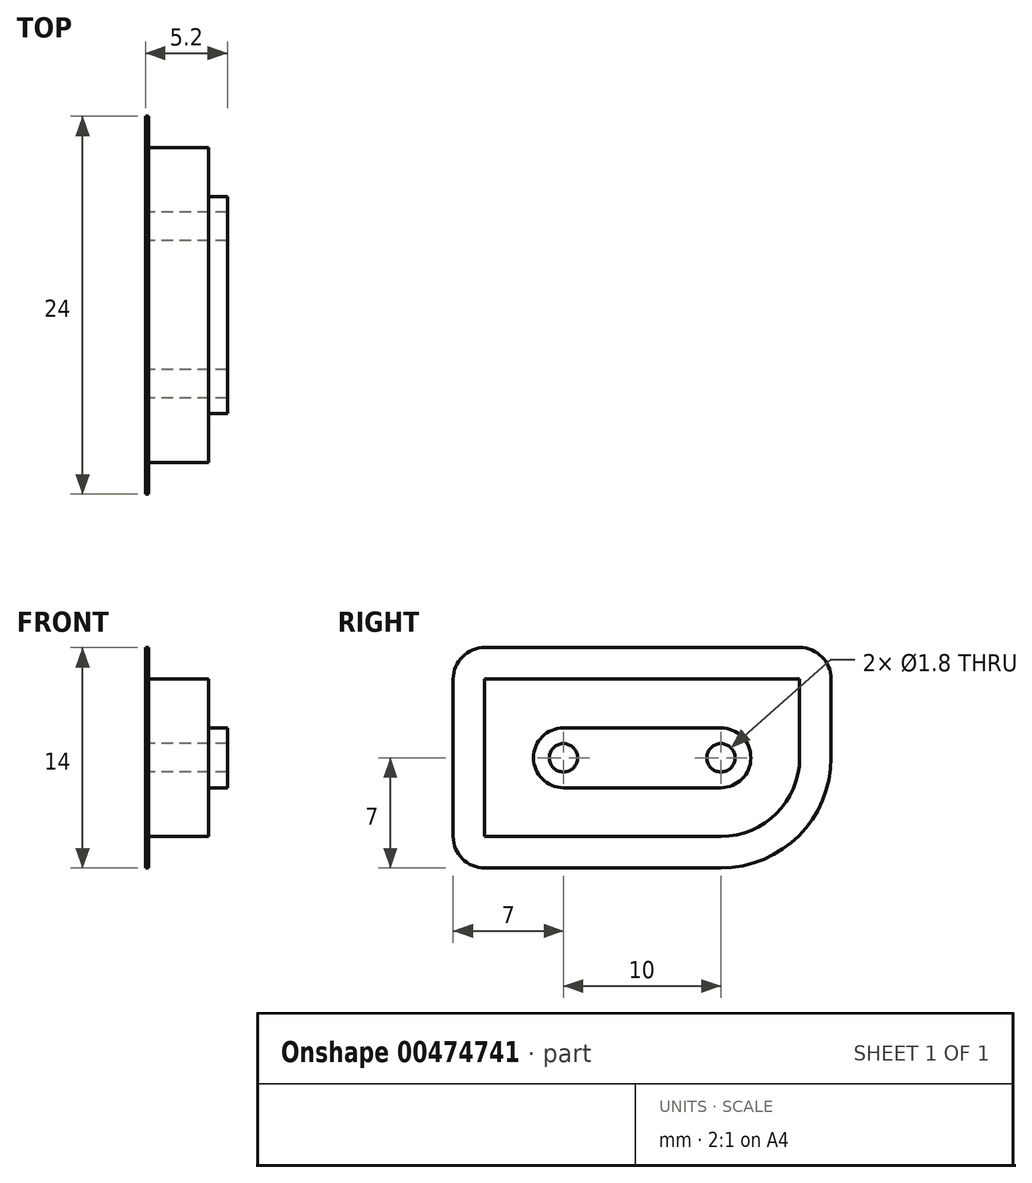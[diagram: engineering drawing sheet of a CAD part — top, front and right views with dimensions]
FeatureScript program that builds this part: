
annotation { "Feature Type Name" : "Feature", "Feature Type Description" : "" }
export const myFeature = defineFeature(function(context is Context, id is Id, definition is map)
    precondition{}
    {
        {
            var Q0;
            Q0=qCreatedBy(makeId("Right.planeOp"),FACE);
            var sketch = newSketch(context, id + "F0", { "sketchPlane" : qUnion([Q0])});
            skCircle(sketch, "E0", {"center": v(5, -5) * mm, "radius": 0.9 * mm});
            skCircle(sketch, "E1", {"center": v(15, -5) * mm, "radius": 0.9 * mm});
            skLineSegment(sketch, "E2", {"start": v(5, -5) * mm, "end": v(15, -5) * mm, "construction": true});
            skLineSegment(sketch, "E3.bottom", {"start": v(0, 0) * mm, "end": v(20, 0) * mm});
            skLineSegment(sketch, "E3.top", {"start": v(0, -10) * mm, "end": v(15, -10) * mm});
            skLineSegment(sketch, "E3.left", {"start": v(0, 0) * mm, "end": v(0, -10) * mm});
            skLineSegment(sketch, "E3.right", {"start": v(20, 0) * mm, "end": v(20, -5) * mm});
            skPoint(sketch, "E4.visualSharp", {"position": v(20, -10) * mm});
            skArc(sketch, "E4.filletArc", {"start": v(15, -10) * mm, "mid": v(18.54, -8.54) * mm, "end": v(20, -5) * mm});
            skSolve(sketch);
        }
        {
            var Q0;
            Q0=qSketchRegion(id+"F0",true);
            extrude(context, id + "F1", {"entities" : qUnion([Q0]), "depth" : 4 * mm, "offsetDistance" : 25 * mm});
        }
        {
            var Q0;
            Q0=makeQuery(id+"F1.opExtrude","CAP_FACE",FACE,{"disambiguationData":[OSD([sQuery(id+"F0.wireOp",EDGE,"E0"),sQuery(id+"F0.wireOp",EDGE,"E1"),sQuery(id+"F0.wireOp",EDGE,"E3.bottom"),sQuery(id+"F0.wireOp",EDGE,"E3.top"),sQuery(id+"F0.wireOp",EDGE,"E3.left"),sQuery(id+"F0.wireOp",EDGE,"E3.right"),sQuery(id+"F0.wireOp",EDGE,"E4.filletArc")])],"isStart":false});
            var sketch = newSketch(context, id + "F2", { "sketchPlane" : qUnion([Q0])});
            skCircle(sketch, "E5", {"center": v(5, -5) * mm, "radius": 0.9 * mm});
            skCircle(sketch, "E6", {"center": v(15, -5) * mm, "radius": 0.9 * mm});
            skLineSegment(sketch, "E7", {"start": v(5, -3.1) * mm, "end": v(15, -3.1) * mm});
            skLineSegment(sketch, "E8", {"start": v(5, -6.9) * mm, "end": v(15, -6.9) * mm});
            skArc(sketch, "E9", {"start": v(5, -3.1) * mm, "mid": v(3.1, -5) * mm, "end": v(5, -6.9) * mm});
            skArc(sketch, "E10", {"start": v(15, -6.9) * mm, "mid": v(16.9, -5) * mm, "end": v(15, -3.1) * mm});
            skSolve(sketch);
        }
        {
            var Q0;
            Q0=qSketchRegion(id+"F2",true);
            extrude(context, id + "F3", {"entities" : qUnion([Q0]), "operationType" : NewBodyOperationType.ADD, "depth" : 1.2 * mm, "offsetDistance" : 25 * mm});
        }
        {
            var Q0;
            Q0=makeQuery(id+"F1.opExtrude","CAP_FACE",FACE,{"disambiguationData":[OSD([sQuery(id+"F0.wireOp",EDGE,"E0"),sQuery(id+"F0.wireOp",EDGE,"E1"),sQuery(id+"F0.wireOp",EDGE,"E3.bottom"),sQuery(id+"F0.wireOp",EDGE,"E3.top"),sQuery(id+"F0.wireOp",EDGE,"E3.left"),sQuery(id+"F0.wireOp",EDGE,"E3.right"),sQuery(id+"F0.wireOp",EDGE,"E4.filletArc")])],"isStart":true});
            var sketch = newSketch(context, id + "F4", { "sketchPlane" : qUnion([Q0])});
            skLineSegment(sketch, "E11", {"start": v(-22, 0) * mm, "end": v(-22, -5) * mm});
            skLineSegment(sketch, "E12", {"start": v(-20, 2) * mm, "end": v(0, 2) * mm});
            skLineSegment(sketch, "E13", {"start": v(2, 0) * mm, "end": v(2, -10) * mm});
            skLineSegment(sketch, "E14", {"start": v(-15, -12) * mm, "end": v(0, -12) * mm});
            skLineSegment(sketch, "E15", {"start": v(-20, 0) * mm, "end": v(0, 0) * mm});
            skLineSegment(sketch, "E16", {"start": v(0, 0) * mm, "end": v(0, -10) * mm});
            skLineSegment(sketch, "E17", {"start": v(0, -10) * mm, "end": v(-15, -10) * mm});
            skLineSegment(sketch, "E18", {"start": v(-20, 0) * mm, "end": v(-20, -5) * mm});
            skArc(sketch, "E19", {"start": v(-20, -5) * mm, "mid": v(-18.54, -8.54) * mm, "end": v(-15, -10) * mm});
            skArc(sketch, "E20", {"start": v(-20, 2) * mm, "mid": v(-21.41, 1.41) * mm, "end": v(-22, 0) * mm});
            skArc(sketch, "E21", {"start": v(-22, -5) * mm, "mid": v(-19.95, -9.95) * mm, "end": v(-15, -12) * mm});
            skArc(sketch, "E22", {"start": v(0, -12) * mm, "mid": v(1.41, -11.41) * mm, "end": v(2, -10) * mm});
            skArc(sketch, "E23", {"start": v(2, 0) * mm, "mid": v(1.41, 1.41) * mm, "end": v(0, 2) * mm});
            skSolve(sketch);
        }
        {
            var Q0;
            Q0 = qSketchRegion(id + "F4", true);
            extrude(context, id + "F5", {"entities" : qUnion([Q0]), "operationType" : NewBodyOperationType.ADD, "oppositeDirection" : true, "depth" : 0.2 * mm, "offsetDistance" : 25 * mm});
        }
    });
